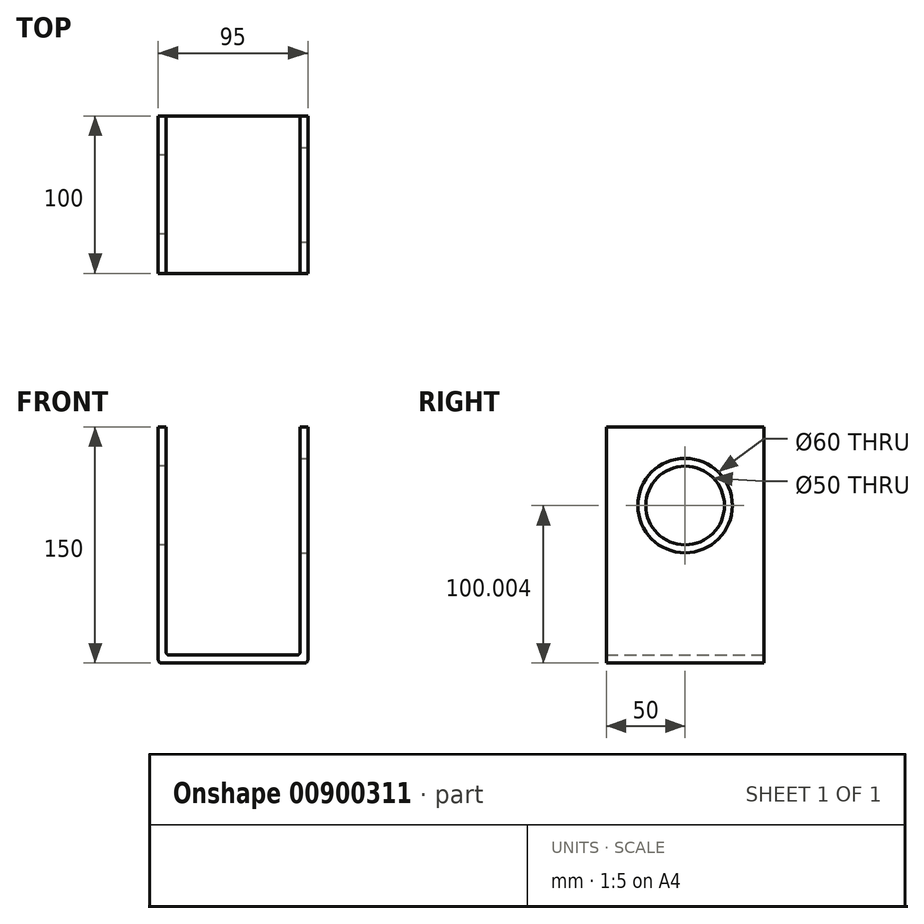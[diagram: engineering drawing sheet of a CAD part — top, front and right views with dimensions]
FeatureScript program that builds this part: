
annotation { "Feature Type Name" : "Feature", "Feature Type Description" : "" }
export const myFeature = defineFeature(function(context is Context, id is Id, definition is map)
    precondition{}
    {
        {
            var Q0;
            Q0=qCreatedBy(makeId("Front.planeOp"),FACE);
            var sketch = newSketch(context, id + "F0", { "sketchPlane" : qUnion([Q0])});
            skLineSegment(sketch, "E0", {"start": v(-58.26, 129.95) * mm, "end": v(-58.26, -18.05) * mm});
            skLineSegment(sketch, "E1", {"start": v(-56.26, -20.05) * mm, "end": v(34.74, -20.05) * mm});
            skLineSegment(sketch, "E2", {"start": v(36.74, -18.05) * mm, "end": v(36.74, 129.95) * mm});
            skLineSegment(sketch, "E3.0", {"start": v(31.74, -13.05) * mm, "end": v(31.74, 129.95) * mm});
            skLineSegment(sketch, "E4.0", {"start": v(-51.26, -15.05) * mm, "end": v(29.74, -15.05) * mm});
            skLineSegment(sketch, "E5.0", {"start": v(-53.26, 129.95) * mm, "end": v(-53.26, -13.05) * mm});
            skLineSegment(sketch, "E6", {"start": v(-58.26, 129.95) * mm, "end": v(-53.26, 129.95) * mm});
            skLineSegment(sketch, "E7", {"start": v(31.74, 129.95) * mm, "end": v(36.74, 129.95) * mm});
            skArc(sketch, "E8.filletArc", {"start": v(29.74, -15.05) * mm, "mid": v(31.15, -14.46) * mm, "end": v(31.74, -13.05) * mm});
            skArc(sketch, "E9.filletArc", {"start": v(-53.26, -13.05) * mm, "mid": v(-52.68, -14.46) * mm, "end": v(-51.26, -15.05) * mm});
            skPoint(sketch, "E10.visualSharp", {"position": v(-58.26, -20.05) * mm});
            skArc(sketch, "E10.filletArc", {"start": v(-58.26, -18.05) * mm, "mid": v(-57.68, -19.46) * mm, "end": v(-56.26, -20.05) * mm});
            skPoint(sketch, "E11.visualSharp", {"position": v(36.74, -20.05) * mm});
            skArc(sketch, "E11.filletArc", {"start": v(34.74, -20.05) * mm, "mid": v(36.15, -19.46) * mm, "end": v(36.74, -18.05) * mm});
            skSolve(sketch);
        }
        {
            var Q0;
            Q0=makeQuery(id+"F0.imprint","IMPRINT",FACE,{"disambiguationData":[TD([[makeQuery(id+"F0.imprint","IMPRINT",EDGE,{"derivedFrom":sQuery(id+"F0.wireOp",EDGE,"E0")}),1.0]])]});
            extrude(context, id + "F1", {"entities" : qUnion([Q0]), "depth" : 100 * mm, "offsetDistance" : 25 * mm});
        }
        {
            var Q0;
            Q0=makeQuery(id+"F1.opExtrude","SWEPT_FACE",FACE,{"disambiguationData":[OSD([sQuery(id+"F0.wireOp",EDGE,"E2")])]});
            var sketch = newSketch(context, id + "F2", { "sketchPlane" : qUnion([Q0])});
            skLineSegment(sketch, "E12", {"start": v(-50, -18.05) * mm, "end": v(-50, -37.34) * mm});
            skLineSegment(sketch, "E13", {"start": v(-50, -18.05) * mm, "end": v(-50, -20.05) * mm});
            skLineSegment(sketch, "E14", {"start": v(-50, -20.05) * mm, "end": v(-50, 79.95) * mm});
            skCircle(sketch, "E15", {"center": v(-50, 79.95) * mm, "radius": 30 * mm});
            skSolve(sketch);
        }
        {
            var Q0;
            Q0=makeQuery(id+"F2.imprint","IMPRINT",FACE,{"disambiguationData":[TD([[makeQuery(id+"F2.imprint","IMPRINT",EDGE,{"derivedFrom":sQuery(id+"F2.wireOp",EDGE,"E15")}),1.0]])]});
            extrude(context, id + "F3", {"entities" : qUnion([Q0]), "operationType" : NewBodyOperationType.REMOVE, "oppositeDirection" : true, "depth" : 5 * mm, "offsetDistance" : 25 * mm});
        }
        {
            var Q0;
            Q0=makeQuery(id+"F1.opExtrude","SWEPT_FACE",FACE,{"disambiguationData":[OSD([sQuery(id+"F0.wireOp",EDGE,"E0")])]});
            var sketch = newSketch(context, id + "F4", { "sketchPlane" : qUnion([Q0])});
            skLineSegment(sketch, "E16", {"start": v(50, -18.05) * mm, "end": v(50, -20.05) * mm});
            skLineSegment(sketch, "E17", {"start": v(50, -20.05) * mm, "end": v(50, 79.95) * mm});
            skCircle(sketch, "E18", {"center": v(50, 79.95) * mm, "radius": 25 * mm});
            skSolve(sketch);
        }
        {
            var Q0;
            Q0=makeQuery(id+"F4.imprint","IMPRINT",FACE,{"disambiguationData":[TD([[makeQuery(id+"F4.imprint","IMPRINT",EDGE,{"derivedFrom":sQuery(id+"F4.wireOp",EDGE,"E18")}),1.0]])]});
            extrude(context, id + "F5", {"entities" : qUnion([Q0]), "operationType" : NewBodyOperationType.REMOVE, "oppositeDirection" : true, "depth" : 5 * mm, "offsetDistance" : 25 * mm});
        }
    });
